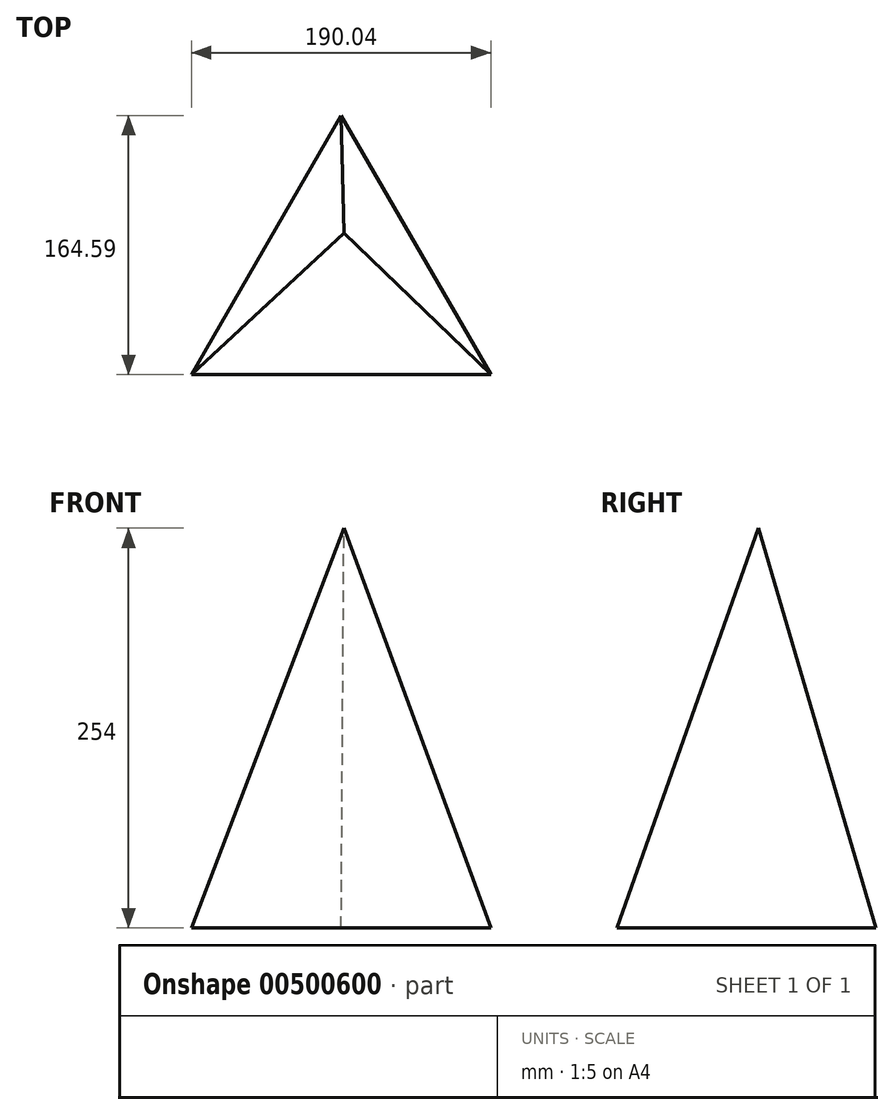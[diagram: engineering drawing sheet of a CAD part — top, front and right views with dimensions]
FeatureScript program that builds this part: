
annotation { "Feature Type Name" : "Feature", "Feature Type Description" : "" }
export const myFeature = defineFeature(function(context is Context, id is Id, definition is map)
    precondition{}
    {
        {
            var Q0;
            Q0=qCreatedBy(makeId("Top.planeOp"),FACE);
            var sketch = newSketch(context, id + "F0", { "sketchPlane" : qUnion([Q0])});
            skCircle(sketch, "E0.cCircle", {"center": v(0, -18.02) * mm, "radius": 109.72 * mm, "construction": true});
            skLineSegment(sketch, "E0.0", {"start": v(0, 91.7) * mm, "end": v(95.02, -72.88) * mm});
            skLineSegment(sketch, "E0.1", {"start": v(95.02, -72.88) * mm, "end": v(-95.02, -72.88) * mm});
            skLineSegment(sketch, "E0.2", {"start": v(-95.02, -72.88) * mm, "end": v(0, 91.7) * mm});
            skSolve(sketch);
        }
        {
            var Q0;
            Q0=qCreatedBy(makeId("Top.planeOp"),FACE);
            cPlane(context, id + "F1", {"entities" : qUnion([Q0]), "cplaneType" : CPlaneType.OFFSET, "offset" : 254 * mm, "width" : 152.4 * mm, "height" : 152.4 * mm});
        }
        {
            var Q0;
            Q0=qCreatedBy(id+"F1.planeOp",FACE);
            var sketch = newSketch(context, id + "F2", { "sketchPlane" : qUnion([Q0])});
            skPoint(sketch, "E1", {"position": v(1.75, 17.05) * mm});
            skSolve(sketch);
        }
        {
            var Q0;
            Q0=makeQuery(id+"F0.imprint","IMPRINT",FACE,{"disambiguationData":[TD([[makeQuery(id+"F0.imprint","IMPRINT",EDGE,{"derivedFrom":sQuery(id+"F0.wireOp",EDGE,"E0.0")}),-1.0]])]});
            var Q1;
            Q1=sQuery(id+"F2.wireOp",VERTEX,"E1");
            loft(context, id + "F3", {"sheetProfilesArray" : [{ "sheetProfileEntities" : qUnion([Q0]) }, { "sheetProfileEntities" : qUnion([Q1]) }]});
        }
    });
